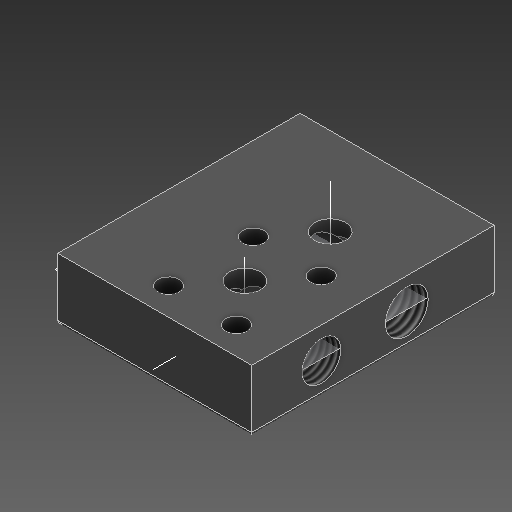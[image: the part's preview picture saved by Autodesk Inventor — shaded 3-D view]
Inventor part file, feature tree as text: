
AUTODESK INVENTOR PART (.ipt)
format: ipt  version: 2021 (Build 250183000, 183)  size: 302,080 bytes
history: native  units: in
note: dims shown in document units (in); Inventor stores cm internally (conversion verified against a paired STEP export)
features: other x12, direct_edit x5, hole x5, move_body x4, plane x3, sketch x3, extrude x2, thread x2, reference x2
ambient origin geometry x8: Origin, YZ Plane, XZ Plane, XY Plane, X Axis, Y Axis, Z Axis, Center Point
bodies: Solid1 (feature_tree)
feature tree (38):
  direct_edit  "Direct Edit1"
  plane  "Work Plane1"
  other  "Work Axis2"
  plane  "Work Plane2"
  extrude  "Extrusion1"  Depth=0.0591in TaperAngle=0.0deg
  plane  "Work Plane3"
  hole  "Hole2"  [1 undecoded]
  extrude  "Extrusion3"  Depth=1.9685in TaperAngle=0.0deg
  sketch  "Sketch4"  dims[d6=0.6184in d7=90.0deg d8=0.0in d9=0.0in d10=0.6299in]
  hole  "Hole6"  [1 undecoded]
  hole  "Hole7"  [1 undecoded]
  hole  "Hole10"  [1 undecoded]
  hole  "Hole12"  [1 undecoded]
  direct_edit  "Direct Edit4"
  direct_edit  "Direct Edit5"
  direct_edit  "Direct Edit6"
  direct_edit  "Direct Edit7"
  thread  "Thread1"  [1 undecoded]
  thread  "Thread3"  [1 undecoded]
  other  "Work Axis1"
  sketch  "Sketch3"  dims[d0=0.0in d1=0.0in d2=0.0591in d3=0.0in d4=0.0in d5=0.0591in]
  other  "Work Axis3"
  sketch  "Sketch6"  dims[d11=0.0in d12=0.0in d13=0.3937in d14=1.9685in d15=0.0in d16=0.315in d17=0.315in d20=0.2362in d28=0.2756in d29=0.2362in d30=0.1575in d31=0.0787in d32=90.0deg d33=1.9685in d34=0.8108in d35=0.4724in d36=1.3189in d37=0.0in d62=0.2362in d63=0.2362in d64=0.1575in d65=0.0787in d66=90.0deg d67=1.5123in d68=0.8108in d69=0.4331in d70=0.2362in d71=0.1575in d72=0.0787in d73=90.0deg d74=0.9449in d75=0.0in d90=0.315in d91=0.2362in d92=0.1575in d93=0.0787in d94=90.0deg d95=1.4961in d96=0.8108in d105=0.3937in d106=0.2362in d107=0.1575in d108=0.0787in d109=90.0deg d110=0.1575in d111=0.0in d112=-0.0394in d113=0.2362in d114=-0.0197in d115=-0.0394in d116=0.3937in d117=0.0in d120=0.3937in d121=0.0in d118=0.5635in d119=0.0295in d122=0.0295in d123=0.0148in]
  reference  "Reference1"
  reference  "Reference2"
  other  "Cut-Extrude26"
  move_body  "Move1"
  move_body  "Move2"
  move_body  "Move3"
  move_body  "Move4"
  parser-record x1  (decoder bookkeeping rows leaked as tree rows — omitted from the tree; the rows remain in map.json)
  other  "BodyV4.iam"
  other  "rotarynozzle:1"
  other  "iner_sleeve:1"
  other  "Size2"
  other  "Size3"
  other  "Size4"
  other  "Size5"
note: 7 required parameter values undecoded (feature->parameter linkage not recoverable at this tier; creation-order binding heuristic only, values carry confidence <= 0.55)
note: 1 file-system path scrubbed to <path> (originals preserved in map.json)
